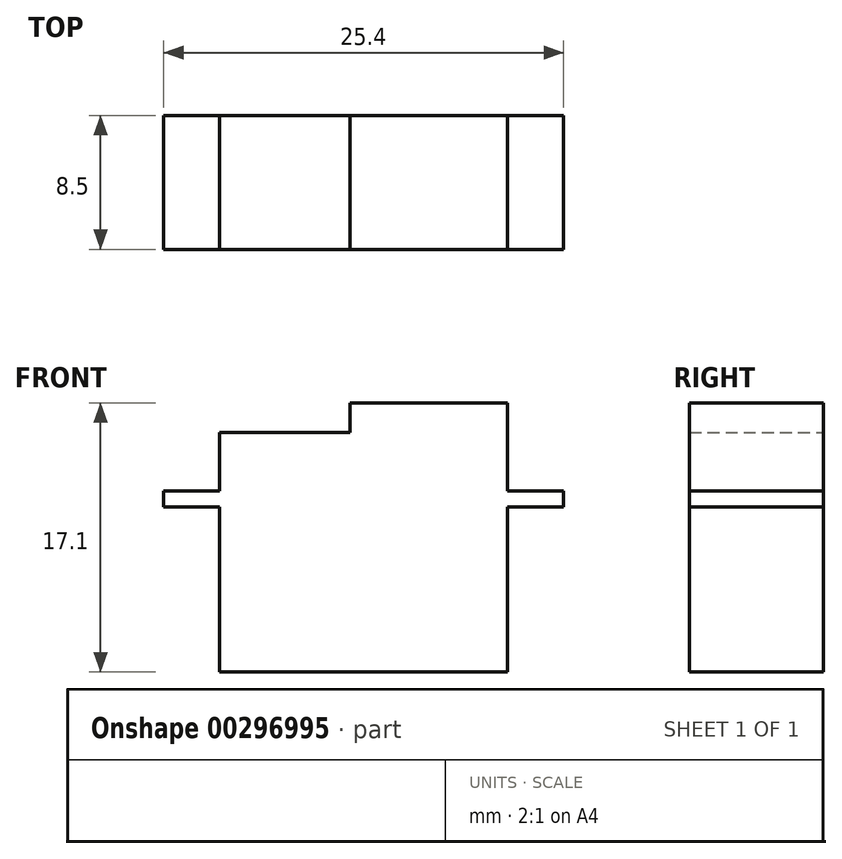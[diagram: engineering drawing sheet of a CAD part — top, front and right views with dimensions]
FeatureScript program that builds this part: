
annotation { "Feature Type Name" : "Feature", "Feature Type Description" : "" }
export const myFeature = defineFeature(function(context is Context, id is Id, definition is map)
    precondition{}
    {
        {
            var Q0;
            Q0=qCreatedBy(makeId("Front.planeOp"),FACE);
            var sketch = newSketch(context, id + "F0", { "sketchPlane" : qUnion([Q0])});
            skLineSegment(sketch, "E0.bottom", {"start": v(0, 4.7) * mm, "end": v(18.3, 4.7) * mm});
            skLineSegment(sketch, "E0.top", {"start": v(0, -10.5) * mm, "end": v(18.3, -10.5) * mm});
            skLineSegment(sketch, "E0.left", {"start": v(0, 4.7) * mm, "end": v(0, -10.5) * mm});
            skLineSegment(sketch, "E0.right", {"start": v(18.3, 4.7) * mm, "end": v(18.3, -10.5) * mm});
            skLineSegment(sketch, "E1.bottom", {"start": v(-3.55, 1) * mm, "end": v(21.85, 1) * mm});
            skLineSegment(sketch, "E1.top", {"start": v(-3.55, 0) * mm, "end": v(21.85, 0) * mm});
            skLineSegment(sketch, "E1.left", {"start": v(-3.55, 1) * mm, "end": v(-3.55, 0) * mm});
            skLineSegment(sketch, "E1.right", {"start": v(21.85, 1) * mm, "end": v(21.85, 0) * mm});
            skLineSegment(sketch, "E2.bottom", {"start": v(8.3, 6.6) * mm, "end": v(18.3, 6.6) * mm});
            skLineSegment(sketch, "E2.top", {"start": v(8.3, 4.7) * mm, "end": v(18.3, 4.7) * mm});
            skLineSegment(sketch, "E2.left", {"start": v(8.3, 6.6) * mm, "end": v(8.3, 4.7) * mm});
            skLineSegment(sketch, "E2.right", {"start": v(18.3, 6.6) * mm, "end": v(18.3, 4.7) * mm});
            skLineSegment(sketch, "E3", {"start": v(9.15, -10.5) * mm, "end": v(9.15, 0) * mm, "construction": true});
            skPoint(sketch, "E4", {"position": v(0, 0) * mm});
            skSolve(sketch);
        }
        {
            var Q0;
            {var subQ0=sQuery(id+"F0.wireOp",EDGE,"E0.top");Q0=makeQuery(id+"F0.imprint","IMPRINT",FACE,{"disambiguationData":[TD([[makeQuery(id+"F0.imprint","IMPRINT",EDGE,{"derivedFrom":subQ0}),1.0]])]});}
            var Q1;
            {var subQ5=sQuery(id+"F0.wireOp",EDGE,"E0.bottom");Q1=makeQuery(id+"F0.imprint","IMPRINT",FACE,{"disambiguationData":[TD([[makeQuery(id+"F0.imprint","IMPRINT",EDGE,{"derivedFrom":subQ5}),-1.0]])]});}
            var Q2;
            Q2=makeQuery(id+"F0.imprint","IMPRINT",FACE,{"disambiguationData":[TD([[makeQuery(id+"F0.imprint","IMPRINT",EDGE,{"derivedFrom":sQuery(id+"F0.wireOp",EDGE,"E2.bottom")}),-1.0]])]});
            var Q3;
            {var subQ5=sQuery(id+"F0.wireOp",EDGE,"E1.left");Q3=makeQuery(id+"F0.imprint","IMPRINT",FACE,{"disambiguationData":[TD([[makeQuery(id+"F0.imprint","IMPRINT",EDGE,{"derivedFrom":subQ5}),1.0]])]});}
            var Q4;
            {var subQ0=sQuery(id+"F0.wireOp",EDGE,"E1.bottom");var subQ1=sQuery(id+"F0.wireOp",EDGE,"E0.left");var subQ2=makeQuery(id+"F0.imprint","INTERSECT",VERTEX,{"derivedFrom":[subQ1,subQ0]});Q4=makeQuery(id+"F0.imprint","IMPRINT",FACE,{"disambiguationData":[TD([[makeQuery(id+"F0.imprint","IMPRINT",EDGE,{"disambiguationData":[TD([[subQ2,-1.0]])],"derivedFrom":subQ1}),1.0]])]});}
            var Q5;
            {var subQ5=sQuery(id+"F0.wireOp",EDGE,"E1.right");Q5=makeQuery(id+"F0.imprint","IMPRINT",FACE,{"disambiguationData":[TD([[makeQuery(id+"F0.imprint","IMPRINT",EDGE,{"derivedFrom":subQ5}),-1.0]])]});}
            extrude(context, id + "F1", {"entities" : qUnion([Q0, Q1, Q2, Q3, Q4, Q5]), "depth" : 8.5 * mm});
        }
    });
